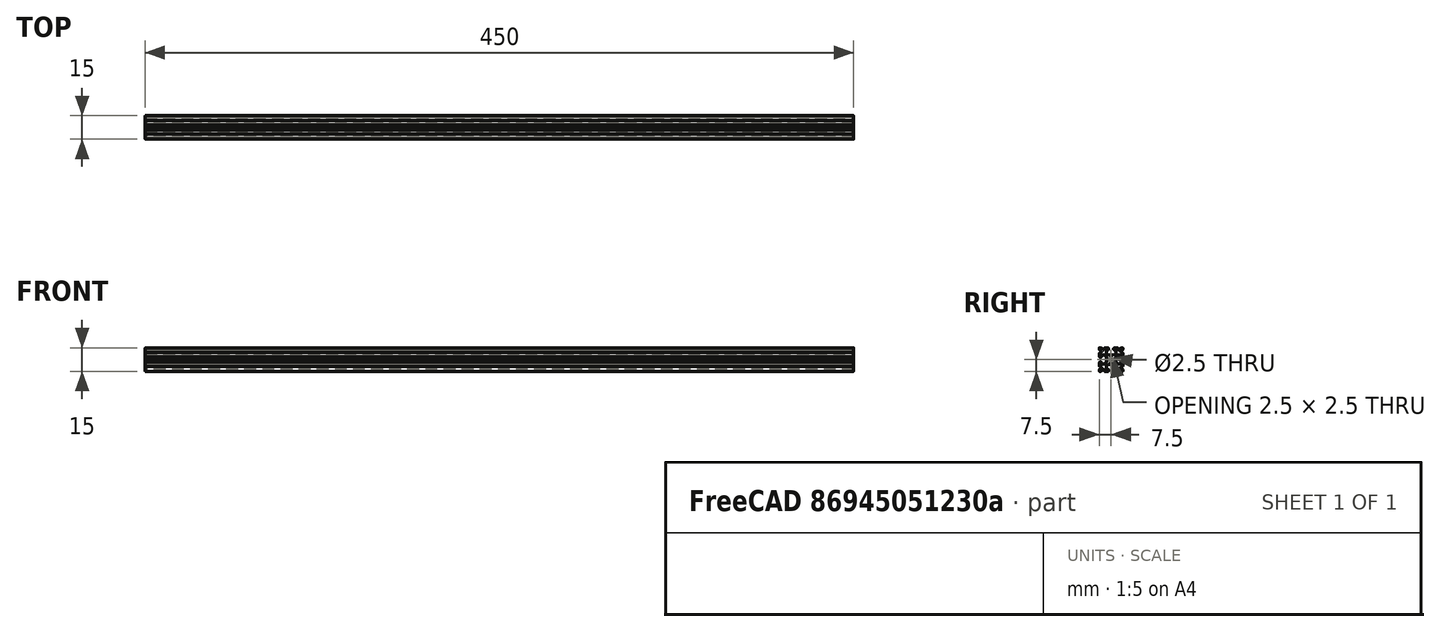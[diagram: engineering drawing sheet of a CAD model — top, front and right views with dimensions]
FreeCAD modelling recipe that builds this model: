
FCSTD DOCUMENT  (FreeCAD 2022.430R26244 +4758 (Git))
Label: as3OpenBeam450mm
License: All rights reserved
LicenseURL: http://en.wikipedia.org/wiki/All_rights_reserved
objects: Part::FeaturePython×9, App::FeaturePython×2
note: 8 computed .brp shape members not serialized (recipe doc carries the construction recipe); baked Part::Feature solids carry a one-line shape summary decoded from their .brp

FEATURE [Part::FeaturePython] b_OpenBeam450mm_001_  label="OpenBeam450mm"  # a2plus imported part (geometry in sourceFile) (typed FeaturePython)
  Placement = pos=(274.93,-178.73,-8.30001) rot=(0,-1,0;1.5708rad)
  TreeRank = 0
  a2p_Version = V0.1
  fixedPosition = false
  objectType = a2pPart
  sourceFile = .\OpenBeam450mm.FCStd
  subassemblyImport = false
  timeLastImport = 1.61981e+09
  updateColors = true
FEATURE [App::FeaturePython] Constraints  # WARN: FeaturePython — macro-defined, semantics opaque (R4)
  TreeRank = 0
  _LinkVersion = 1
  _Version = 1
FEATURE [Part::FeaturePython] Parts  # WARN: FeaturePython — macro-defined, semantics opaque (R4)
  Group = -> [b_OpenBeam450mm_001_]
  GroupMode = 0
  TreeRank = 0
  _LinkVersion = 1
FEATURE [Part::FeaturePython] Assembly  label="As3OpenBeam450mm"  # WARN: FeaturePython — macro-defined, semantics opaque (R4)
  AutoRelax = true
  BuildShape = 0
  Freeze = false
  Group = -> [Constraints,Elements,Parts]
  TreeRank = 0
  Verbose = false
  _LinkVersion = 1
  _SolverType = 1
  _Version = 1
FEATURE [App::FeaturePython] Elements  # WARN: FeaturePython — macro-defined, semantics opaque (R4)
  Group = -> [Element,Element001,Element002,Element003,Element004,Element005]
  TreeRank = 0
  _LinkVersion = 1
FEATURE [Part::FeaturePython] Element  label="Extrem1"  # link proxy (typed FeaturePython)
  Detach = false
  LinkTransform = true
  LinkedObject = -> b_OpenBeam450mm_001_ [Face16]
  TreeRank = 0
  _LinkVersion = 1
  _Parent = -> Elements
FEATURE [Part::FeaturePython] Element001  label="FaceHoriz1"  # link proxy (typed FeaturePython)
  Detach = false
  LinkTransform = true
  LinkedObject = -> b_OpenBeam450mm_001_ [Face18]
  TreeRank = 0
  _LinkVersion = 1
  _Parent = -> Elements
FEATURE [Part::FeaturePython] Element002  label="FaceLat1"  # link proxy (typed FeaturePython)
  Detach = false
  LinkTransform = true
  LinkedObject = -> b_OpenBeam450mm_001_ [Face5]
  TreeRank = 0
  _LinkVersion = 1
  _Parent = -> Elements
FEATURE [Part::FeaturePython] Element003  label="FaceHoriz2"  # link proxy (typed FeaturePython)
  Detach = false
  LinkTransform = true
  LinkedObject = -> b_OpenBeam450mm_001_ [Face20]
  TreeRank = 0
  _LinkVersion = 1
  _Parent = -> Elements
FEATURE [Part::FeaturePython] Element004  label="Extrem2"  # link proxy (typed FeaturePython)
  Detach = false
  LinkTransform = true
  LinkedObject = -> b_OpenBeam450mm_001_ [Face17]
  TreeRank = 0
  _LinkVersion = 1
  _Parent = -> Elements
FEATURE [Part::FeaturePython] Element005  label="FaceLat2"  # link proxy (typed FeaturePython)
  Detach = false
  LinkTransform = true
  LinkedObject = -> b_OpenBeam450mm_001_ [Face8]
  TreeRank = 0
  _LinkVersion = 1
  _Parent = -> Elements
